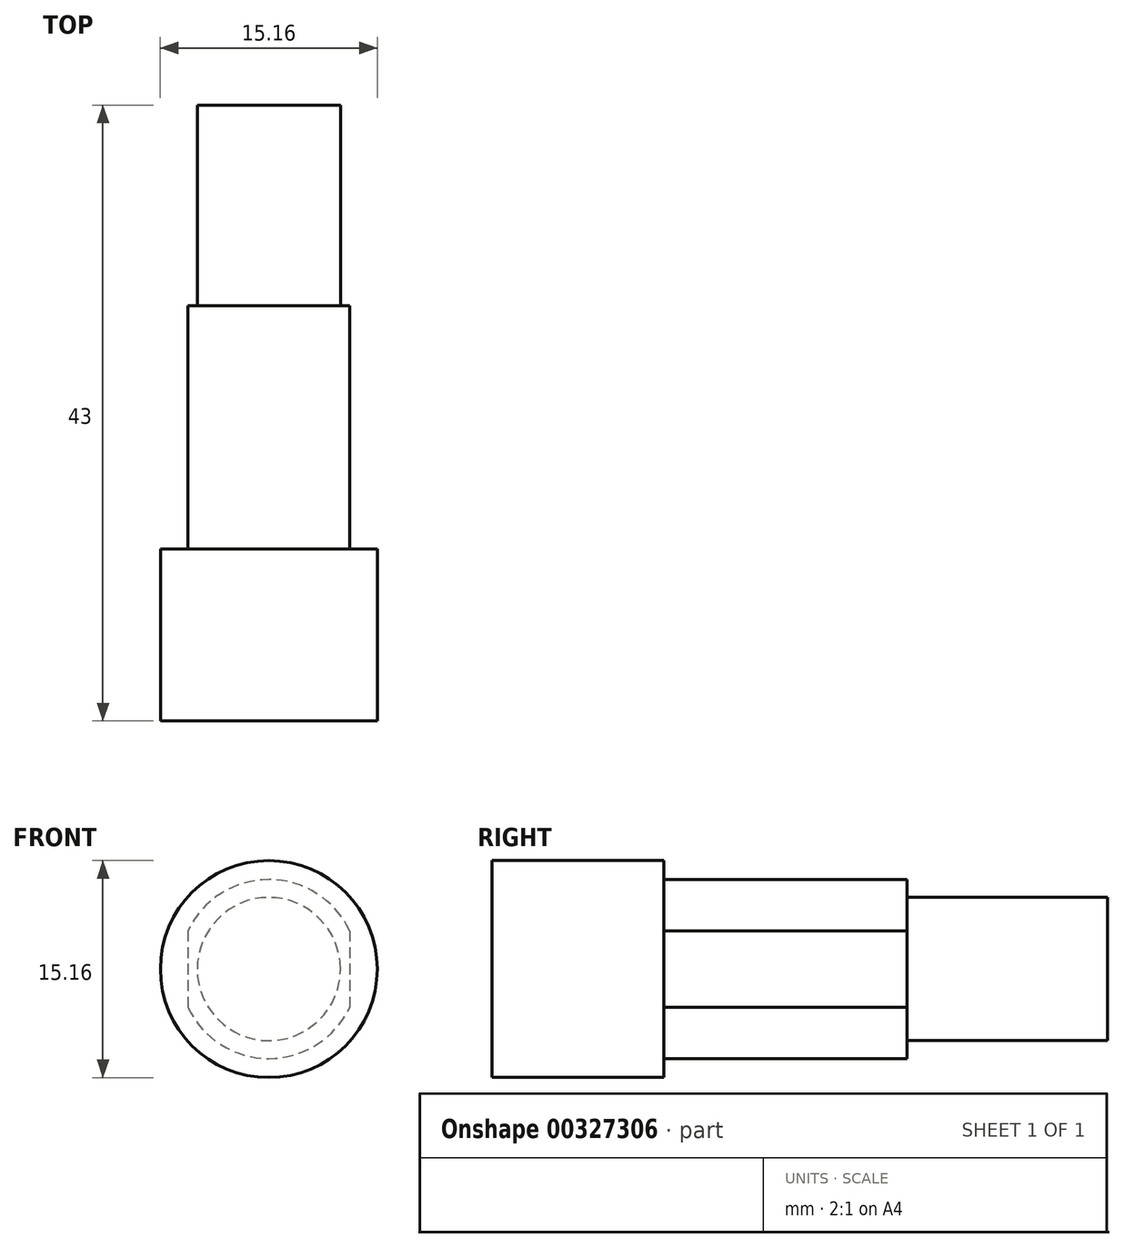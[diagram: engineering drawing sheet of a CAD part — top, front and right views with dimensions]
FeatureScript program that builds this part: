
annotation { "Feature Type Name" : "Feature", "Feature Type Description" : "" }
export const myFeature = defineFeature(function(context is Context, id is Id, definition is map)
    precondition{}
    {
        {
            var Q0;
            Q0=qCreatedBy(makeId("Front.planeOp"),FACE);
            var sketch = newSketch(context, id + "F0", { "sketchPlane" : qUnion([Q0])});
            skCircle(sketch, "E0", {"center": v(0, 0) * mm, "radius": 6.25 * mm});
            skSolve(sketch);
        }
        {
            var Q0;
            Q0 = qSketchRegion(id + "F0", true);
            extrude(context, id + "F1", {"entities" : qUnion([Q0]), "depth" : 17 * mm, "offsetDistance" : 25 * mm});
        }
        {
            var Q0;
            Q0=makeQuery(id+"F1.opExtrude","CAP_FACE",FACE,{"disambiguationData":[OSD([sQuery(id+"F0.wireOp",EDGE,"E0")])],"isStart":false});
            var sketch = newSketch(context, id + "F2", { "sketchPlane" : qUnion([Q0])});
            skCircle(sketch, "E1", {"center": v(0, 0) * mm, "radius": 7.58 * mm});
            skSolve(sketch);
        }
        {
            var Q0;
            Q0 = qSketchRegion(id + "F2", true);
            extrude(context, id + "F3", {"entities" : qUnion([Q0]), "operationType" : NewBodyOperationType.ADD, "depth" : 12 * mm, "offsetDistance" : 25 * mm});
        }
        {
            var Q0;
            Q0=makeQuery(id+"F1.opExtrude","CAP_FACE",FACE,{"disambiguationData":[OSD([sQuery(id+"F0.wireOp",EDGE,"E0")])],"isStart":true});
            var sketch = newSketch(context, id + "F4", { "sketchPlane" : qUnion([Q0])});
            skLineSegment(sketch, "E2.bottom", {"start": v(-5.65, 7.5) * mm, "end": v(5.65, 7.5) * mm});
            skLineSegment(sketch, "E2.top", {"start": v(-5.65, -7.5) * mm, "end": v(5.65, -7.5) * mm});
            skLineSegment(sketch, "E2.left", {"start": v(-5.65, 7.5) * mm, "end": v(-5.65, -7.5) * mm});
            skLineSegment(sketch, "E2.right", {"start": v(5.65, 7.5) * mm, "end": v(5.65, -7.5) * mm});
            skPoint(sketch, "E2.middle", {"position": v(0, 0) * mm});
            skLineSegment(sketch, "E3.bottom", {"start": v(-5.65, 7.5) * mm, "end": v(-10.65, 7.5) * mm});
            skLineSegment(sketch, "E3.top", {"start": v(-5.65, -7.5) * mm, "end": v(-10.65, -7.5) * mm});
            skLineSegment(sketch, "E3.right", {"start": v(-10.65, 7.5) * mm, "end": v(-10.65, -7.5) * mm});
            skLineSegment(sketch, "E4.bottom", {"start": v(5.65, 7.5) * mm, "end": v(10.65, 7.5) * mm});
            skLineSegment(sketch, "E4.top", {"start": v(5.65, -7.5) * mm, "end": v(10.65, -7.5) * mm});
            skLineSegment(sketch, "E4.right", {"start": v(10.65, 7.5) * mm, "end": v(10.65, -7.5) * mm});
            skSolve(sketch);
        }
        {
            var Q0;
            {var subQ0=sQuery(id+"F4.wireOp",EDGE,"E2.left");var subQ1=makeQuery(id+"F1.opExtrude","CAP_EDGE",EDGE,{"disambiguationData":[OSD([sQuery(id+"F0.wireOp",EDGE,"E0")])],"isStart":true});var subQ2=makeQuery(id+"F4.imprint","INTERSECT",VERTEX,{"disambiguationData":[OD(0.0)],"derivedFrom":[subQ1,subQ0]});Q0=makeQuery(id+"F4.imprint","IMPRINT",FACE,{"disambiguationData":[TD([[makeQuery(id+"F4.imprint","IMPRINT",EDGE,{"disambiguationData":[TD([[subQ2,-1.0]])],"derivedFrom":subQ0}),-1.0]])]});}
            var Q1;
            {var subQ0=sQuery(id+"F4.wireOp",EDGE,"E2.right");var subQ1=makeQuery(id+"F1.opExtrude","CAP_EDGE",EDGE,{"disambiguationData":[OSD([sQuery(id+"F0.wireOp",EDGE,"E0")])],"isStart":true});var subQ2=makeQuery(id+"F4.imprint","INTERSECT",VERTEX,{"disambiguationData":[OD(0.0)],"derivedFrom":[subQ1,subQ0]});Q1=makeQuery(id+"F4.imprint","IMPRINT",FACE,{"disambiguationData":[TD([[makeQuery(id+"F4.imprint","IMPRINT",EDGE,{"disambiguationData":[TD([[subQ2,-1.0]])],"derivedFrom":subQ0}),1.0]])]});}
            var Q2;
            Q2=makeQuery(id+"F3.opExtrude","CAP_FACE",FACE,{"disambiguationData":[OSD([sQuery(id+"F2.wireOp",EDGE,"E1")])],"isStart":true});
            extrude(context, id + "F5", {"entities" : qUnion([Q0, Q1]), "operationType" : NewBodyOperationType.REMOVE, "endBound" : BoundingType.UP_TO_SURFACE, "oppositeDirection" : true, "depth" : 25 * mm, "endBoundEntityFace" : qUnion([Q2]), "offsetDistance" : 25 * mm});
        }
        {
            var Q0;
            Q0=makeQuery(id+"F1.opExtrude","CAP_FACE",FACE,{"disambiguationData":[OSD([sQuery(id+"F0.wireOp",EDGE,"E0")])],"isStart":true});
            var sketch = newSketch(context, id + "F6", { "sketchPlane" : qUnion([Q0])});
            skCircle(sketch, "E5", {"center": v(0, 0) * mm, "radius": 5 * mm});
            skSolve(sketch);
        }
        {
            var Q0;
            Q0 = qSketchRegion(id + "F6", true);
            extrude(context, id + "F7", {"entities" : qUnion([Q0]), "operationType" : NewBodyOperationType.ADD, "depth" : 14 * mm, "offsetDistance" : 25 * mm});
        }
    });
